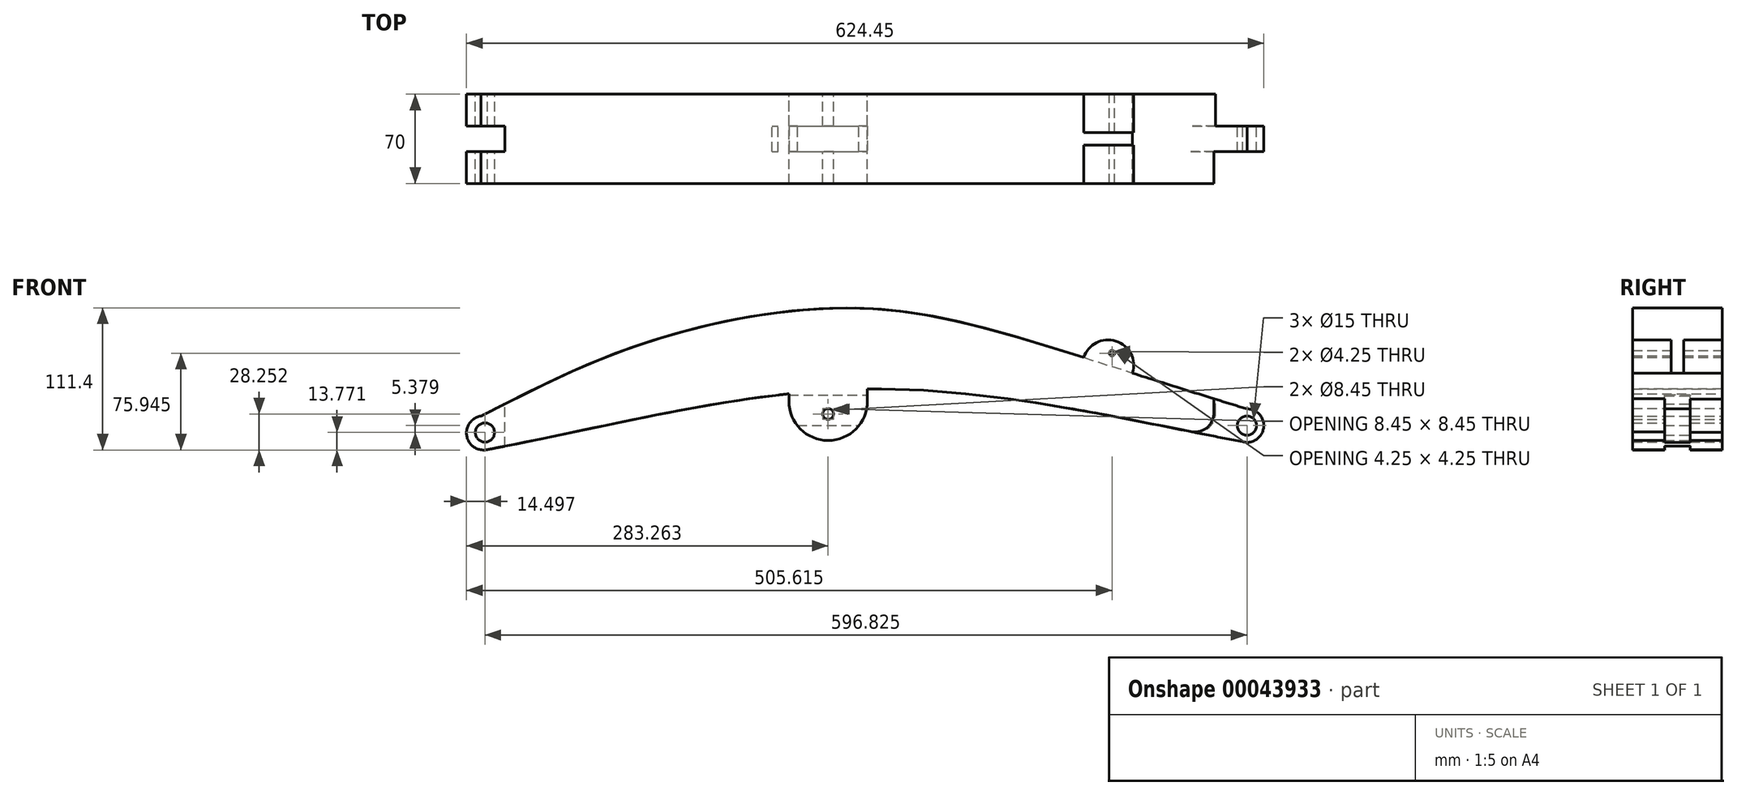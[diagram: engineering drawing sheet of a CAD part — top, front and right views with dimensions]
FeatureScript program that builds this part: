
annotation { "Feature Type Name" : "Feature", "Feature Type Description" : "" }
export const myFeature = defineFeature(function(context is Context, id is Id, definition is map)
    precondition{}
    {
        {
            var Q0;
            Q0=qCreatedBy(makeId("Front.planeOp"),FACE);
            var sketch = newSketch(context, id + "F0", { "sketchPlane" : qUnion([Q0])});
            skLineSegment(sketch, "E0", {"start": v(0, 0) * mm, "end": v(600, 0) * mm, "construction": true});
            skLineSegment(sketch, "E1", {"start": v(0, 0) * mm, "end": v(300, 0) * mm, "construction": true});
            skLineSegment(sketch, "E2", {"start": v(300, 0) * mm, "end": v(300, 92) * mm, "construction": true});
            skFitSpline(sketch, "E3", {"points": [v(0, 0) * mm, v(300, 92) * mm, v(600, 0) * mm], "startDerivative": vector(688.15, 373.34) * mm, "endDerivative": vector(1153.14, -341.46) * mm, "construction": true});
            skFitSpline(sketch, "E4", {"points": [v(0, 0) * mm, v(300, 28.66) * mm, v(600, 0) * mm], "startDerivative": vector(600, 119.3) * mm, "endDerivative": vector(600, -119.3) * mm, "construction": true});
            skPoint(sketch, "E5", {"position": v(300, 46) * mm});
            skLineSegment(sketch, "E6", {"start": v(0, 0) * mm, "end": v(0, 7.5) * mm, "construction": true});
            skLineSegment(sketch, "E7", {"start": v(0, 0) * mm, "end": v(5.04, -18.82) * mm, "construction": true});
            skArc(sketch, "E8", {"start": v(0, 7.5) * mm, "mid": v(-11.1, -8.27) * mm, "end": v(5.04, -18.82) * mm});
            skLineSegment(sketch, "E9", {"start": v(600, 0) * mm, "end": v(596.6, -12.66) * mm, "construction": true});
            skLineSegment(sketch, "E10", {"start": v(600, 0) * mm, "end": v(600, 13.11) * mm, "construction": true});
            skArc(sketch, "E11", {"start": v(596.6, -12.66) * mm, "mid": v(613, -1.71) * mm, "end": v(600, 13.11) * mm});
            skFitSpline(sketch, "E12", {"points": [v(0, 7.5) * mm, v(131.42, 65.71) * mm, v(300, 92) * mm, v(600, 13.11) * mm], "startDerivative": vector(537.47, 272.8) * mm, "endDerivative": vector(1109.45, -337.2) * mm});
            skFitSpline(sketch, "E13", {"points": [v(5.04, -18.82) * mm, v(300, 28.66) * mm, v(596.6, -12.66) * mm], "startDerivative": vector(595.14, 113.3) * mm, "endDerivative": vector(595.01, -113.74) * mm});
            skSolve(sketch);
        }
        {
            var Q0;
            Q0 = qSketchRegion(id + "F0", true);
            extrude(context, id + "F1", {"entities" : qUnion([Q0]), "depth" : 70 * mm});
        }
        {
            var Q0;
            Q0=qCreatedBy(makeId("Front.planeOp"),FACE);
            var sketch = newSketch(context, id + "F2", { "sketchPlane" : qUnion([Q0])});
            skCircle(sketch, "E14", {"center": v(3.16, -5.38) * mm, "radius": 7.5 * mm});
            skCircle(sketch, "E15", {"center": v(599.98, 0) * mm, "radius": 7.5 * mm});
            skSolve(sketch);
        }
        {
            var Q0;
            Q0 = qSketchRegion(id + "F2", true);
            extrude(context, id + "F3", {"entities" : qUnion([Q0]), "operationType" : NewBodyOperationType.REMOVE, "depth" : 70 * mm});
        }
        {
            var Q0;
            Q0=qCreatedBy(makeId("Top.planeOp"),FACE);
            var sketch = newSketch(context, id + "F4", { "sketchPlane" : qUnion([Q0])});
            skLineSegment(sketch, "E16", {"start": v(613.64, 0) * mm, "end": v(613.64, -70) * mm, "construction": true});
            skLineSegment(sketch, "E17.bottom", {"start": v(613.64, 0) * mm, "end": v(575.3, 0) * mm});
            skLineSegment(sketch, "E17.top", {"start": v(613.64, -25) * mm, "end": v(575.3, -25) * mm});
            skLineSegment(sketch, "E17.left", {"start": v(613.64, 0) * mm, "end": v(613.64, -25) * mm});
            skLineSegment(sketch, "E17.right", {"start": v(575.3, 0) * mm, "end": v(575.3, -25) * mm});
            skLineSegment(sketch, "E18.bottom", {"start": v(613.64, -70) * mm, "end": v(574.04, -70) * mm});
            skLineSegment(sketch, "E18.top", {"start": v(613.64, -45) * mm, "end": v(574.04, -45) * mm});
            skLineSegment(sketch, "E18.left", {"start": v(613.64, -70) * mm, "end": v(613.64, -45) * mm});
            skLineSegment(sketch, "E18.right", {"start": v(574.04, -70) * mm, "end": v(574.04, -45) * mm});
            skLineSegment(sketch, "E19", {"start": v(-11.86, 0) * mm, "end": v(-11.86, -70) * mm, "construction": true});
            skLineSegment(sketch, "E20.bottom", {"start": v(-11.86, -25) * mm, "end": v(18.64, -25) * mm});
            skLineSegment(sketch, "E20.top", {"start": v(-11.86, -45) * mm, "end": v(18.64, -45) * mm});
            skLineSegment(sketch, "E20.left", {"start": v(-11.86, -25) * mm, "end": v(-11.86, -45) * mm});
            skLineSegment(sketch, "E20.right", {"start": v(18.64, -25) * mm, "end": v(18.64, -45) * mm});
            skSolve(sketch);
        }
        {
            var Q0;
            Q0 = qSketchRegion(id + "F4", true);
            extrude(context, id + "F5", {"entities" : qUnion([Q0]), "operationType" : NewBodyOperationType.REMOVE, "oppositeDirection" : true, "depth" : 25 * mm, "hasSecondDirection" : true, "secondDirectionOppositeDirection" : false, "secondDirectionDepth" : 25 * mm});
        }
        {
            var Q0;
            Q0=makeQuery(id+"F5.boolean.opBoolean","INTERSECT",EDGE,{"derivedFrom":[makeQuery(id+"F1.opExtrude","SWEPT_FACE",FACE,{"disambiguationData":[OSD([sQuery(id+"F0.wireOp",EDGE,"E13")])]}),makeQuery(id+"F5.opExtrude","SWEPT_FACE",FACE,{"disambiguationData":[OSD([sQuery(id+"F4.wireOp",EDGE,"E18.right")])]})]});
            var Q1;
            Q1=makeQuery(id+"F5.boolean.opBoolean","INTERSECT",EDGE,{"derivedFrom":[makeQuery(id+"F1.opExtrude","SWEPT_FACE",FACE,{"disambiguationData":[OSD([sQuery(id+"F0.wireOp",EDGE,"E13")])]}),makeQuery(id+"F5.opExtrude","SWEPT_FACE",FACE,{"disambiguationData":[OSD([sQuery(id+"F4.wireOp",EDGE,"E17.right")])]})]});
            fillet(context, id + "F6", {"entities" : qUnion([Q0, Q1]), "radius" : 15 * mm, "tangentPropagation" : true, "allowEdgeOverflow" : false});
        }
        {
            var Q0;
            Q0=qCreatedBy(makeId("Front.planeOp"),FACE);
            var sketch = newSketch(context, id + "F7", { "sketchPlane" : qUnion([Q0])});
            skLineSegment(sketch, "E21.bottom", {"start": v(241.18, 30.44) * mm, "end": v(302.66, 30.44) * mm});
            skLineSegment(sketch, "E21.top", {"start": v(241.18, 19.1) * mm, "end": v(302.66, 19.1) * mm});
            skLineSegment(sketch, "E21.left", {"start": v(241.18, 30.44) * mm, "end": v(241.18, 19.1) * mm});
            skLineSegment(sketch, "E21.right", {"start": v(302.66, 30.44) * mm, "end": v(302.66, 19.1) * mm});
            skArc(sketch, "E22", {"start": v(241.18, 19.1) * mm, "mid": v(271.92, -11.64) * mm, "end": v(302.66, 19.1) * mm});
            skLineSegment(sketch, "E23", {"start": v(271.92, 19.1) * mm, "end": v(271.92, 9.1) * mm, "construction": true});
            skCircle(sketch, "E24", {"center": v(271.92, 9.1) * mm, "radius": 4.22 * mm});
            skLineSegment(sketch, "E25", {"start": v(0, 0) * mm, "end": v(260, 0) * mm, "construction": true});
            skLineSegment(sketch, "E26", {"start": v(260, 0) * mm, "end": v(271.92, 9.1) * mm, "construction": true});
            skSolve(sketch);
        }
        {
            var Q0;
            Q0 = qSketchRegion(id + "F7", true);
            extrude(context, id + "F8", {"entities" : qUnion([Q0]), "operationType" : NewBodyOperationType.ADD, "depth" : 70 * mm});
        }
        {
            var Q0;
            Q0=qCreatedBy(makeId("Top.planeOp"),FACE);
            var sketch = newSketch(context, id + "F9", { "sketchPlane" : qUnion([Q0])});
            skLineSegment(sketch, "E27.bottom", {"start": v(228, -45) * mm, "end": v(328, -45) * mm});
            skLineSegment(sketch, "E27.top", {"start": v(228, -25) * mm, "end": v(328, -25) * mm});
            skLineSegment(sketch, "E27.left", {"start": v(228, -45) * mm, "end": v(228, -25) * mm});
            skLineSegment(sketch, "E27.right", {"start": v(328, -45) * mm, "end": v(328, -25) * mm});
            skLineSegment(sketch, "E28", {"start": v(0, 0) * mm, "end": v(0, -70) * mm, "construction": true});
            skLineSegment(sketch, "E29", {"start": v(0, 0) * mm, "end": v(228, 0) * mm});
            skSolve(sketch);
        }
        {
            var Q0;
            Q0 = qSketchRegion(id + "F9", true);
            extrude(context, id + "F10", {"entities" : qUnion([Q0]), "operationType" : NewBodyOperationType.REMOVE, "depth" : 24 * mm});
        }
        {
            var Q0;
            Q0=qCreatedBy(makeId("Front.planeOp"),FACE);
            var sketch = newSketch(context, id + "F11", { "sketchPlane" : qUnion([Q0])});
            skFitSpline(sketch, "E30.0", {"points": [v(0, 7.5) * mm, v(50.35, 33.05) * mm, v(124.57, 70.43) * mm, v(325.56, 110.92) * mm, v(447.33, 59.51) * mm, v(600, 13.11) * mm], "construction": true});
            skLineSegment(sketch, "E31", {"start": v(575.3, 20.69) * mm, "end": v(491.25, 47.26) * mm});
            skArc(sketch, "E32", {"start": v(510.32, 41.23) * mm, "mid": v(497.3, 66.33) * mm, "end": v(472.2, 53.33) * mm});
            skLineSegment(sketch, "E33", {"start": v(472.2, 53.33) * mm, "end": v(510.32, 41.23) * mm});
            skLineSegment(sketch, "E34", {"start": v(491.25, 47.26) * mm, "end": v(494.28, 56.8) * mm, "construction": true});
            skCircle(sketch, "E35", {"center": v(494.28, 56.8) * mm, "radius": 2.12 * mm});
            skLineSegment(sketch, "E36", {"start": v(472.2, 53.33) * mm, "end": v(471, 49.6) * mm});
            skLineSegment(sketch, "E37", {"start": v(471, 49.6) * mm, "end": v(509.05, 37.49) * mm});
            skLineSegment(sketch, "E38", {"start": v(509.05, 37.49) * mm, "end": v(510.32, 41.23) * mm});
            skSolve(sketch);
        }
        {
            var Q0;
            Q0 = qSketchRegion(id + "F11", true);
            extrude(context, id + "F12", {"entities" : qUnion([Q0]), "operationType" : NewBodyOperationType.ADD, "depth" : 70 * mm});
        }
        {
            var Q0;
            Q0=makeQuery(id+"F12.boolean.opBoolean","MERGE",FACE,{"derivedFrom":[makeQuery(id+"F8.boolean.opBoolean","MERGE",FACE,{"derivedFrom":[makeQuery(id+"F1.opExtrude","CAP_FACE",FACE,{"disambiguationData":[OSD([sQuery(id+"F0.wireOp",EDGE,"E8"),sQuery(id+"F0.wireOp",EDGE,"E11"),sQuery(id+"F0.wireOp",EDGE,"E12"),sQuery(id+"F0.wireOp",EDGE,"E13")])],"isStart":true}),makeQuery(id+"F8.opExtrude","CAP_FACE",FACE,{"disambiguationData":[OSD([sQuery(id+"F7.wireOp",EDGE,"E21.bottom"),sQuery(id+"F7.wireOp",EDGE,"E21.left"),sQuery(id+"F7.wireOp",EDGE,"E21.right"),sQuery(id+"F7.wireOp",EDGE,"E22"),sQuery(id+"F7.wireOp",EDGE,"E24")])],"isStart":true})]}),makeQuery(id+"F12.opExtrude","CAP_FACE",FACE,{"disambiguationData":[OSD([sQuery(id+"F11.wireOp",EDGE,"E32"),sQuery(id+"F11.wireOp",EDGE,"E35"),sQuery(id+"F11.wireOp",EDGE,"E36"),sQuery(id+"F11.wireOp",EDGE,"E37"),sQuery(id+"F11.wireOp",EDGE,"E38")])],"isStart":true})]});
            cPlane(context, id + "F13", {"entities" : qUnion([Q0]), "cplaneType" : CPlaneType.OFFSET, "offset" : 30 * mm, "oppositeDirection" : true, "width" : 150 * mm, "height" : 150 * mm});
        }
        {
            var Q0;
            Q0=qCreatedBy(id+"F13.planeOp",FACE);
            var sketch = newSketch(context, id + "F14", { "sketchPlane" : qUnion([Q0])});
            skArc(sketch, "E39.0", {"start": v(-510.32, 41.23) * mm, "mid": v(-497.3, 66.33) * mm, "end": v(-472.2, 53.33) * mm});
            skCircle(sketch, "E39.1", {"center": v(-494.28, 56.8) * mm, "radius": 2.12 * mm});
            skLineSegment(sketch, "E40", {"start": v(-472.2, 53.33) * mm, "end": v(-510.32, 41.23) * mm});
            skSolve(sketch);
        }
        {
            var Q0;
            Q0 = qSketchRegion(id + "F14", true);
            extrude(context, id + "F15", {"entities" : qUnion([Q0]), "operationType" : NewBodyOperationType.REMOVE, "oppositeDirection" : true, "depth" : 10 * mm});
        }
    });
